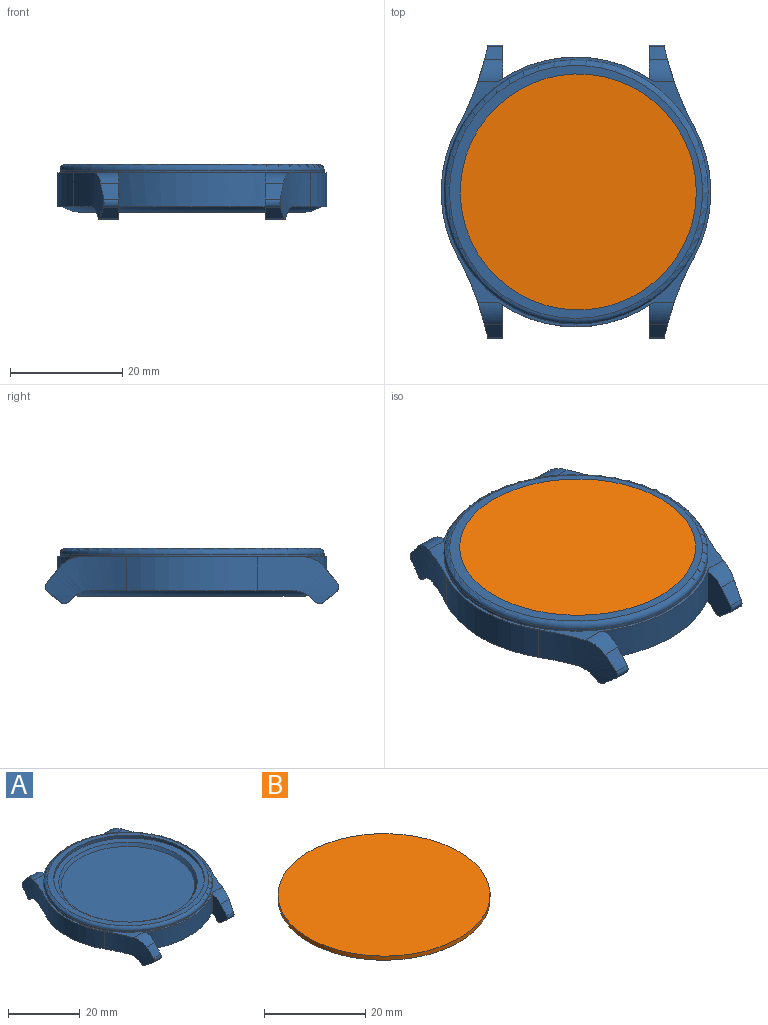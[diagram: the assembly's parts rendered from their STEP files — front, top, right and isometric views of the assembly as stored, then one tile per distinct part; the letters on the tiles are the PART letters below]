
ASSEMBLY  parts=2 mates=1
PART A: 55 faces, bbox 51x52.2x9.8 mm
  f0: cylinder r=24mm len=3mm, axis (0,0,-1), area 0.7mm2, adj f1,f10,f11
  f1: plane 8.3x5.94mm, normal (1,0,0), area 32.7mm2, adj f0,f3,f5,f6,f7,f8,f9,f10
  f2: cylinder r=52mm len=14.54mm, axis (0,0,-1), area 90.8mm2, adj f3,f4,f5,f6,f7,f8,f9,f10
  f3: plane 3.26x2.84mm, normal (0,0.77,0.63), area 10.9mm2, adj f1,f2,f5,f6
  f4: plane 48x48mm, normal (0,0,1), area 111.6mm2, adj f2,f5,f12,f15,f17,f23,f26,f28
  f5: cylinder r=5mm len=4.43mm, axis (1,0,0), area 16.5mm2, adj f1,f2,f3,f4,f23
  f6: cylinder r=1.06mm len=2.74mm, axis (1,0,0), area 4.5mm2, adj f1,f2,f3,f7
  f7: plane 3.31x2.37mm, normal (0,0.63,-0.77), area 9.2mm2, adj f1,f2,f6,f8
  f8: cylinder r=1mm len=3.67mm, axis (1,0,0), area 5.1mm2, adj f1,f2,f7,f9
  f9: plane 3.88x0.69mm, normal (0,-0.69,-0.72), area 3.6mm2, adj f1,f2,f8,f10
  f10: cylinder r=5mm len=5.08mm, axis (1,0,0), area 13.6mm2, adj f0,f1,f2,f9,f11
  f11: plane 48x48mm, normal (0,0,-1), area 164.4mm2, adj f0,f2,f10,f12,f13,f15,f21,f23
  f12: cylinder r=24mm len=23.15mm, axis (0,0,-1), area 144.9mm2, adj f2,f4,f11,f26
  f13: cylinder r=24mm len=3mm, axis (0,0,-1), area 0.7mm2, adj f11,f14,f21
  f14: plane 8.3x5.94mm, normal (-1,0,0), area 32.7mm2, adj f13,f16,f17,f18,f19,f20,f21,f22
  f15: cylinder r=52mm len=14.54mm, axis (0,0,-1), area 90.8mm2, adj f4,f11,f16,f17,f18,f19,f20,f21
  f16: plane 3.26x2.84mm, normal (0,0.77,0.63), area 10.9mm2, adj f14,f15,f17,f22
  f17: cylinder r=5mm len=4.43mm, axis (1,0,0), area 16.5mm2, adj f4,f14,f15,f16,f23
  f18: plane 3.31x2.37mm, normal (0,0.63,-0.77), area 9.2mm2, adj f14,f15,f19,f22
  f19: cylinder r=1mm len=3.67mm, axis (1,0,0), area 5.1mm2, adj f14,f15,f18,f20
  f20: plane 3.88x0.69mm, normal (0,-0.69,-0.72), area 3.6mm2, adj f14,f15,f19,f21
  f21: cylinder r=5mm len=5.08mm, axis (1,0,0), area 13.6mm2, adj f11,f13,f14,f15,f20
  f22: cylinder r=1.06mm len=2.74mm, axis (1,0,0), area 4.5mm2, adj f14,f15,f16,f18
  f23: cylinder r=24mm len=27.48mm, axis (0,0,-1), area 164.9mm2, adj f1,f4,f5,f11,f14,f17
  f24: cylinder r=24mm len=3mm, axis (0,0,-1), area 0.7mm2, adj f11,f25,f29
  f25: plane 8.3x5.94mm, normal (1,0,0), area 32.7mm2, adj f24,f27,f28,f29,f30,f31,f32,f33
  f26: cylinder r=52mm len=14.54mm, axis (0,0,-1), area 90.8mm2, adj f4,f11,f12,f27,f28,f29,f30,f31
  f27: plane 3.26x2.84mm, normal (0,-0.77,0.63), area 10.9mm2, adj f25,f26,f28,f33
  f28: cylinder r=5mm len=4.43mm, axis (1,0,0), area 16.5mm2, adj f4,f25,f26,f27,f45
  f29: cylinder r=5mm len=5.08mm, axis (1,0,0), area 13.6mm2, adj f11,f24,f25,f26,f30
  f30: plane 3.88x0.69mm, normal (0,0.69,-0.72), area 3.6mm2, adj f25,f26,f29,f31
  f31: cylinder r=1mm len=3.67mm, axis (1,0,0), area 5.1mm2, adj f25,f26,f30,f32
  f32: plane 3.31x2.37mm, normal (0,-0.63,-0.77), area 9.2mm2, adj f25,f26,f31,f33
  f33: cylinder r=1.06mm len=2.74mm, axis (1,0,0), area 4.5mm2, adj f25,f26,f27,f32
  f34: cylinder r=24mm len=23.15mm, axis (0,0,-1), area 144.9mm2, adj f4,f11,f15,f37
  f35: cylinder r=24mm len=3mm, axis (0,0,-1), area 0.7mm2, adj f11,f36,f41
  f36: plane 8.3x5.94mm, normal (-1,0,0), area 32.7mm2, adj f35,f38,f39,f40,f41,f42,f43,f44
  f37: cylinder r=52mm len=14.54mm, axis (0,0,-1), area 90.8mm2, adj f4,f11,f34,f38,f39,f40,f41,f42
  f38: plane 3.26x2.84mm, normal (0,-0.77,0.63), area 10.9mm2, adj f36,f37,f39,f40
  f39: cylinder r=5mm len=4.43mm, axis (1,0,0), area 16.5mm2, adj f4,f36,f37,f38,f45
  f40: cylinder r=1.06mm len=2.74mm, axis (1,0,0), area 4.5mm2, adj f36,f37,f38,f44
  f41: cylinder r=5mm len=5.08mm, axis (1,0,0), area 13.6mm2, adj f11,f35,f36,f37,f42
  f42: plane 3.88x0.69mm, normal (0,0.69,-0.72), area 3.6mm2, adj f36,f37,f41,f43
  f43: cylinder r=1mm len=3.67mm, axis (1,0,0), area 5.1mm2, adj f36,f37,f42,f44
  f44: plane 3.31x2.37mm, normal (0,-0.63,-0.77), area 9.2mm2, adj f36,f37,f40,f43
  f45: cylinder r=24mm len=27.48mm, axis (0,0,-1), area 164.9mm2, adj f4,f11,f25,f28,f36,f39
  f46: plane 40x40mm, normal (0,0,-1), area 1256.6mm2, adj f47
  f47: torus R=20mm, axis (0,0,1), area 435.7mm2, adj f11,f46
  f48: cylinder r=23.5mm len=47mm, axis (0,0,-1), area 73.8mm2, adj f4,f50
  f49: plane 45x45mm, normal (0,0,1), area 205mm2, adj f50,f52
  f50: torus R=22.5mm, axis (0,0,1), area 228.3mm2, adj f48,f49
  f51: plane 42x42mm, normal (0,0,1), area 215.3mm2, adj f52,f54
  f52: cylinder r=21mm len=42mm, axis (0,0,1), area 131.9mm2, adj f49,f51
  f53: plane 37.2x37.2mm, normal (0,0,1), area 1086.8mm2, adj f54
  f54: cone r=20mm half-angle=35deg, axis (0,0,1), area 145.4mm2, adj f51,f53
PART B: 3 faces, bbox 42x42x1 mm
  f0: cylinder r=21mm len=42mm, axis (0,0,-1), area 131.9mm2, adj f1,f2
  f1: plane 42x42mm, normal (0,0,1), area 1385.4mm2, adj f0
  f2: plane 42x42mm, normal (0,0,-1), area 1385.4mm2, adj f0
PLACE A t=(-12.21,-4.56,-3.14)mm
PLACE B t=(-11.81,-4.56,6.36)mm
MATE fastened B.f0 <-> A.f52  axis (0,0,1) through (-11.81,-4.56,7.36)mm
